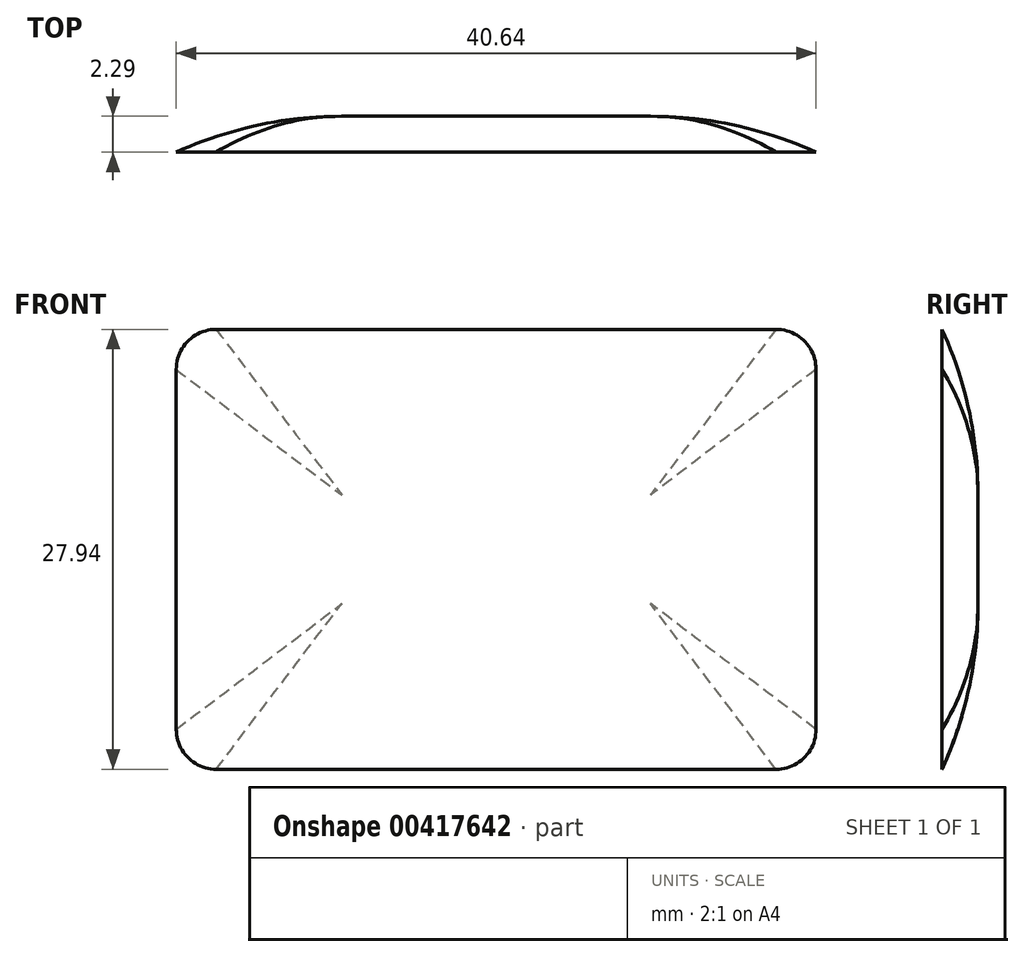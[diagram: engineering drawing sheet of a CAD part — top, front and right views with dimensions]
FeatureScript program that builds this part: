
annotation { "Feature Type Name" : "Feature", "Feature Type Description" : "" }
export const myFeature = defineFeature(function(context is Context, id is Id, definition is map)
    precondition{}
    {
        {
            var Q0;
            Q0=qCreatedBy(makeId("Front.planeOp"),FACE);
            var sketch = newSketch(context, id + "F0", { "sketchPlane" : qUnion([Q0])});
            skLineSegment(sketch, "E0.bottom", {"start": v(-6.82, 19.84) * mm, "end": v(-47.46, 19.84) * mm});
            skLineSegment(sketch, "E0.top", {"start": v(-6.82, 47.78) * mm, "end": v(-47.46, 47.78) * mm});
            skLineSegment(sketch, "E0.left", {"start": v(-6.82, 19.84) * mm, "end": v(-6.82, 47.78) * mm});
            skLineSegment(sketch, "E0.right", {"start": v(-47.46, 19.84) * mm, "end": v(-47.46, 47.78) * mm});
            skSolve(sketch);
        }
        {
            var Q0;
            Q0 = qSketchRegion(id + "F0", true);
            extrude(context, id + "F1", {"entities" : qUnion([Q0]), "depth" : 2.3 * mm});
        }
        {
            var Q0;
            Q0=makeQuery(id+"F1.opExtrude","SWEPT_EDGE",EDGE,{"disambiguationData":[OSD([sQuery(id+"F0.wireOp",EDGE,"E0.top"),sQuery(id+"F0.wireOp",EDGE,"E0.left")])]});
            var Q1;
            Q1=makeQuery(id+"F1.opExtrude","SWEPT_EDGE",EDGE,{"disambiguationData":[OSD([sQuery(id+"F0.wireOp",EDGE,"E0.top"),sQuery(id+"F0.wireOp",EDGE,"E0.right")])]});
            var Q2;
            Q2=makeQuery(id+"F1.opExtrude","SWEPT_EDGE",EDGE,{"disambiguationData":[OSD([sQuery(id+"F0.wireOp",EDGE,"E0.bottom"),sQuery(id+"F0.wireOp",EDGE,"E0.right")])]});
            var Q3;
            Q3=makeQuery(id+"F1.opExtrude","SWEPT_EDGE",EDGE,{"disambiguationData":[OSD([sQuery(id+"F0.wireOp",EDGE,"E0.bottom"),sQuery(id+"F0.wireOp",EDGE,"E0.left")])]});
            fillet(context, id + "F2", {"entities" : qUnion([Q0, Q1, Q2, Q3]), "radius" : 2.54 * mm, "tangentPropagation" : true, "allowEdgeOverflow" : false});
        }
        {
            var Q0;
            Q0=makeQuery(id+"F1.opExtrude","CAP_EDGE",EDGE,{"disambiguationData":[OSD([sQuery(id+"F0.wireOp",EDGE,"E0.top")])],"isStart":true});
            fillet(context, id + "F3", {"entities" : qUnion([Q0]), "radius" : 25.4 * mm, "tangentPropagation" : true, "allowEdgeOverflow" : false});
        }
    });
